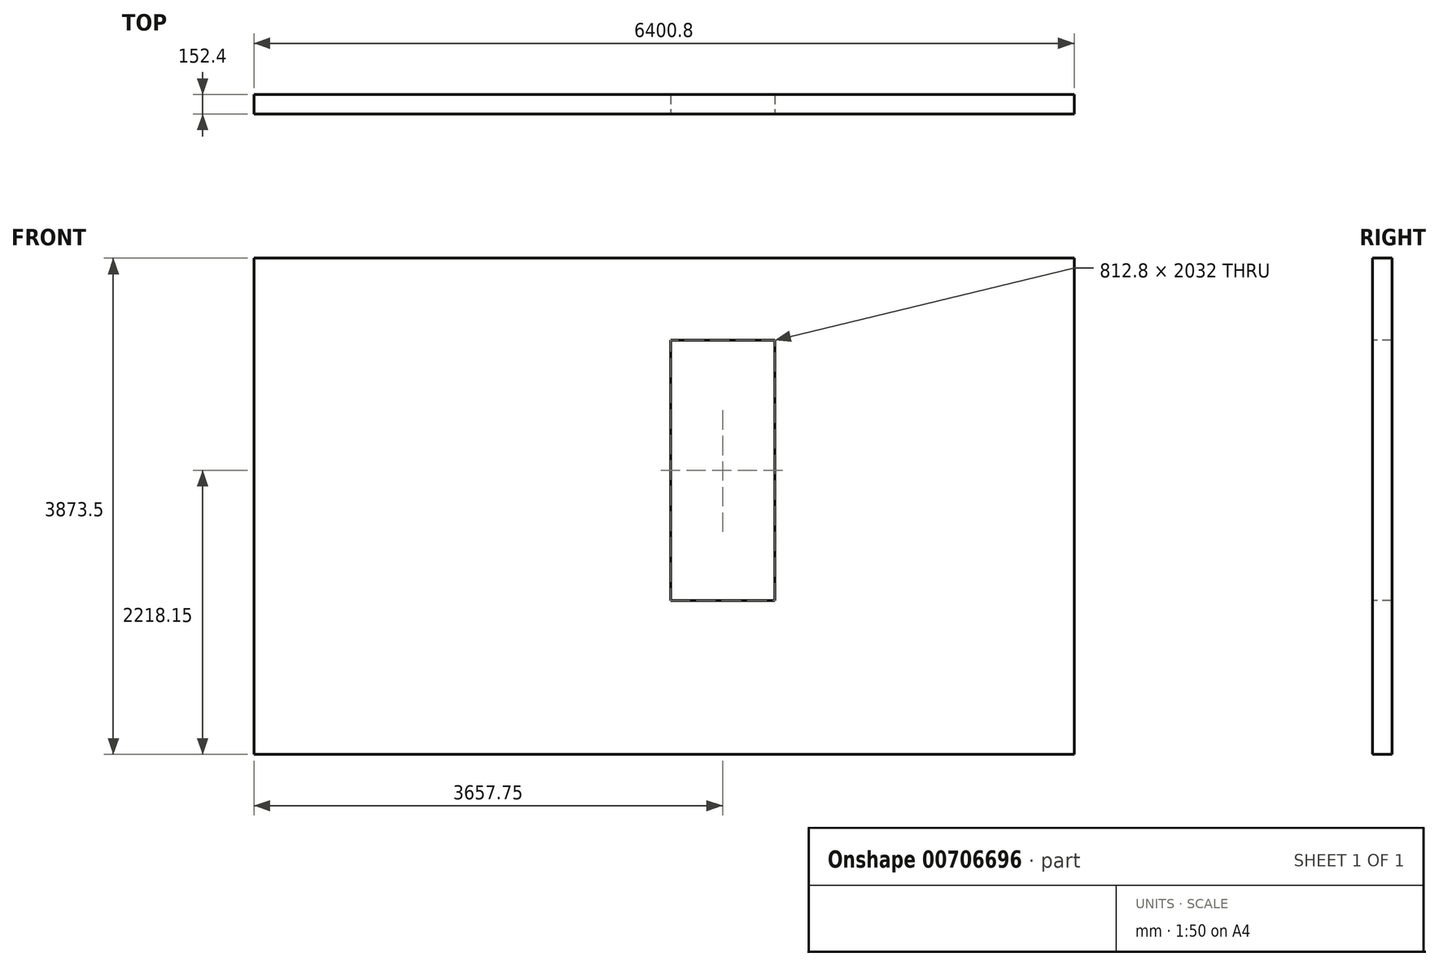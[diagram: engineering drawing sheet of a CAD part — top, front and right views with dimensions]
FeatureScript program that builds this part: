
annotation { "Feature Type Name" : "Feature", "Feature Type Description" : "" }
export const myFeature = defineFeature(function(context is Context, id is Id, definition is map)
    precondition{}
    {
        {
            var Q0;
            Q0=qCreatedBy(makeId("Front.planeOp"),FACE);
            var sketch = newSketch(context, id + "F0", { "sketchPlane" : qUnion([Q0])});
            skLineSegment(sketch, "E0.bottom", {"start": v(0, 0) * mm, "end": v(6400.8, 0) * mm});
            skLineSegment(sketch, "E0.top", {"start": v(0, 3873.5) * mm, "end": v(6400.8, 3873.5) * mm});
            skLineSegment(sketch, "E0.left", {"start": v(0, 0) * mm, "end": v(0, 3873.5) * mm});
            skLineSegment(sketch, "E0.right", {"start": v(6400.8, 0) * mm, "end": v(6400.8, 3873.5) * mm});
            skSolve(sketch);
        }
        {
            var Q0;
            Q0=makeQuery(id+"F0.imprint","IMPRINT",FACE,{"disambiguationData":[TD([[makeQuery(id+"F0.imprint","IMPRINT",EDGE,{"derivedFrom":sQuery(id+"F0.wireOp",EDGE,"E0.bottom")}),1.0]])]});
            extrude(context, id + "F1", {"entities" : qUnion([Q0]), "depth" : 152.4 * mm, "offsetDistance" : 25.4 * mm});
        }
        {
            var Q0;
            Q0=makeQuery(id+"F1.opExtrude","CAP_FACE",FACE,{"disambiguationData":[OSD([sQuery(id+"F0.wireOp",EDGE,"E0.bottom"),sQuery(id+"F0.wireOp",EDGE,"E0.top"),sQuery(id+"F0.wireOp",EDGE,"E0.left"),sQuery(id+"F0.wireOp",EDGE,"E0.right")])],"isStart":false});
            var sketch = newSketch(context, id + "F2", { "sketchPlane" : qUnion([Q0])});
            skLineSegment(sketch, "E1.bottom", {"start": v(3251.35, 3234.15) * mm, "end": v(4064.15, 3234.15) * mm});
            skLineSegment(sketch, "E1.top", {"start": v(3251.35, 1202.15) * mm, "end": v(4064.15, 1202.15) * mm});
            skLineSegment(sketch, "E1.left", {"start": v(3251.35, 3234.15) * mm, "end": v(3251.35, 1202.15) * mm});
            skLineSegment(sketch, "E1.right", {"start": v(4064.15, 3234.15) * mm, "end": v(4064.15, 1202.15) * mm});
            skSolve(sketch);
        }
        {
            var Q0;
            Q0=makeQuery(id+"F2.imprint","IMPRINT",FACE,{"disambiguationData":[TD([[makeQuery(id+"F2.imprint","IMPRINT",EDGE,{"derivedFrom":sQuery(id+"F2.wireOp",EDGE,"E1.bottom")}),-1.0]])]});
            extrude(context, id + "F3", {"entities" : qUnion([Q0]), "operationType" : NewBodyOperationType.REMOVE, "oppositeDirection" : true, "depth" : 152.4 * mm, "offsetDistance" : 25.4 * mm});
        }
        {
            var Q0;
            Q0=makeQuery(id+"F1.opExtrude","CAP_FACE",FACE,{"disambiguationData":[OSD([sQuery(id+"F0.wireOp",EDGE,"E0.bottom"),sQuery(id+"F0.wireOp",EDGE,"E0.top"),sQuery(id+"F0.wireOp",EDGE,"E0.left"),sQuery(id+"F0.wireOp",EDGE,"E0.right")])],"isStart":false});
            var sketch = newSketch(context, id + "F4", { "sketchPlane" : qUnion([Q0])});
            skLineSegment(sketch, "E2.bottom", {"start": v(0, 0) * mm, "end": v(1549.4, 0) * mm});
            skLineSegment(sketch, "E2.top", {"start": v(0, 0) * mm, "end": v(1549.4, 0) * mm});
            skLineSegment(sketch, "E2.left", {"start": v(0, 0) * mm, "end": v(0, 0) * mm});
            skLineSegment(sketch, "E2.right", {"start": v(1549.4, 0) * mm, "end": v(1549.4, 0) * mm});
            skSolve(sketch);
        }
    });
